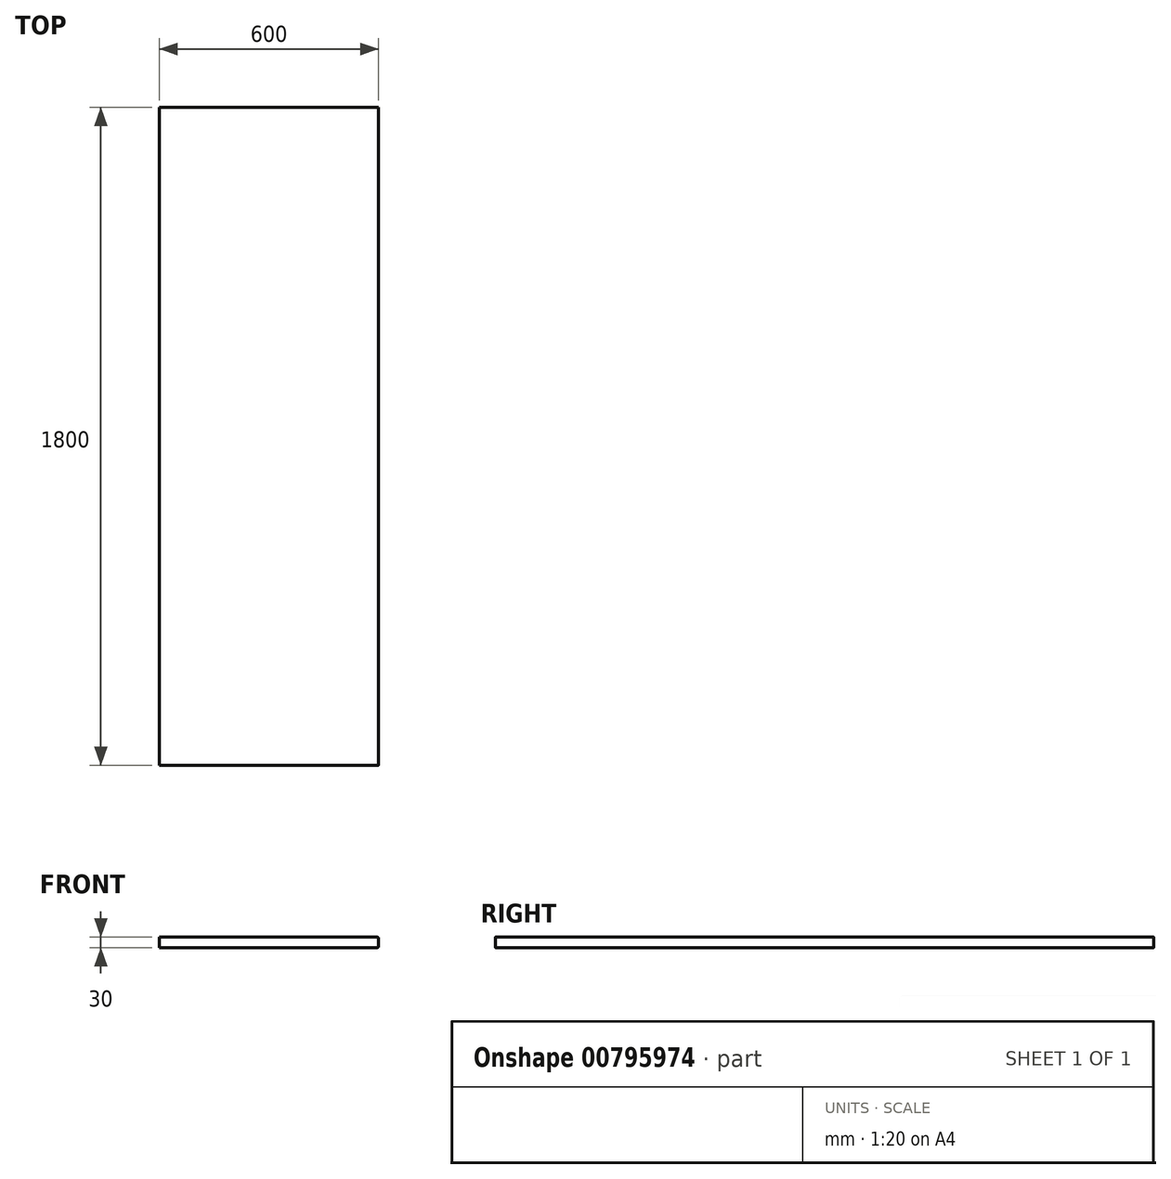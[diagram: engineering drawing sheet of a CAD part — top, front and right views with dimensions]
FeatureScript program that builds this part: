
annotation { "Feature Type Name" : "Feature", "Feature Type Description" : "" }
export const myFeature = defineFeature(function(context is Context, id is Id, definition is map)
    precondition{}
    {
        {
            var Q0;
            Q0=qCreatedBy(makeId("Top.planeOp"),FACE);
            var sketch = newSketch(context, id + "F0", { "sketchPlane" : qUnion([Q0])});
            skLineSegment(sketch, "E0.bottom", {"start": v(0, 0) * mm, "end": v(600, 0) * mm});
            skLineSegment(sketch, "E0.top", {"start": v(0, 1800) * mm, "end": v(600, 1800) * mm});
            skLineSegment(sketch, "E0.left", {"start": v(0, 0) * mm, "end": v(0, 1800) * mm});
            skLineSegment(sketch, "E0.right", {"start": v(600, 0) * mm, "end": v(600, 1800) * mm});
            skSolve(sketch);
        }
        {
            var Q0;
            Q0=makeQuery(id+"F0.imprint","IMPRINT",FACE,{"disambiguationData":[TD([[makeQuery(id+"F0.imprint","IMPRINT",EDGE,{"derivedFrom":sQuery(id+"F0.wireOp",EDGE,"E0.bottom")}),1.0]])]});
            extrude(context, id + "F1", {"entities" : qUnion([Q0]), "depth" : 30 * mm, "offsetDistance" : 25 * mm});
        }
        {
            var Q0;
            Q0=makeQuery(id+"F1.opExtrude","CAP_EDGE",EDGE,{"disambiguationData":[OSD([sQuery(id+"F0.wireOp",EDGE,"E0.right")])],"isStart":false});
            var Q1;
            Q1=makeQuery(id+"F1.opExtrude","CAP_EDGE",EDGE,{"disambiguationData":[OSD([sQuery(id+"F0.wireOp",EDGE,"E0.right")])],"isStart":true});
            fillet(context, id + "F2", {"entities" : qUnion([Q0, Q1]), "radius" : 5 * mm, "tangentPropagation" : true, "allowEdgeOverflow" : false});
        }
    });
